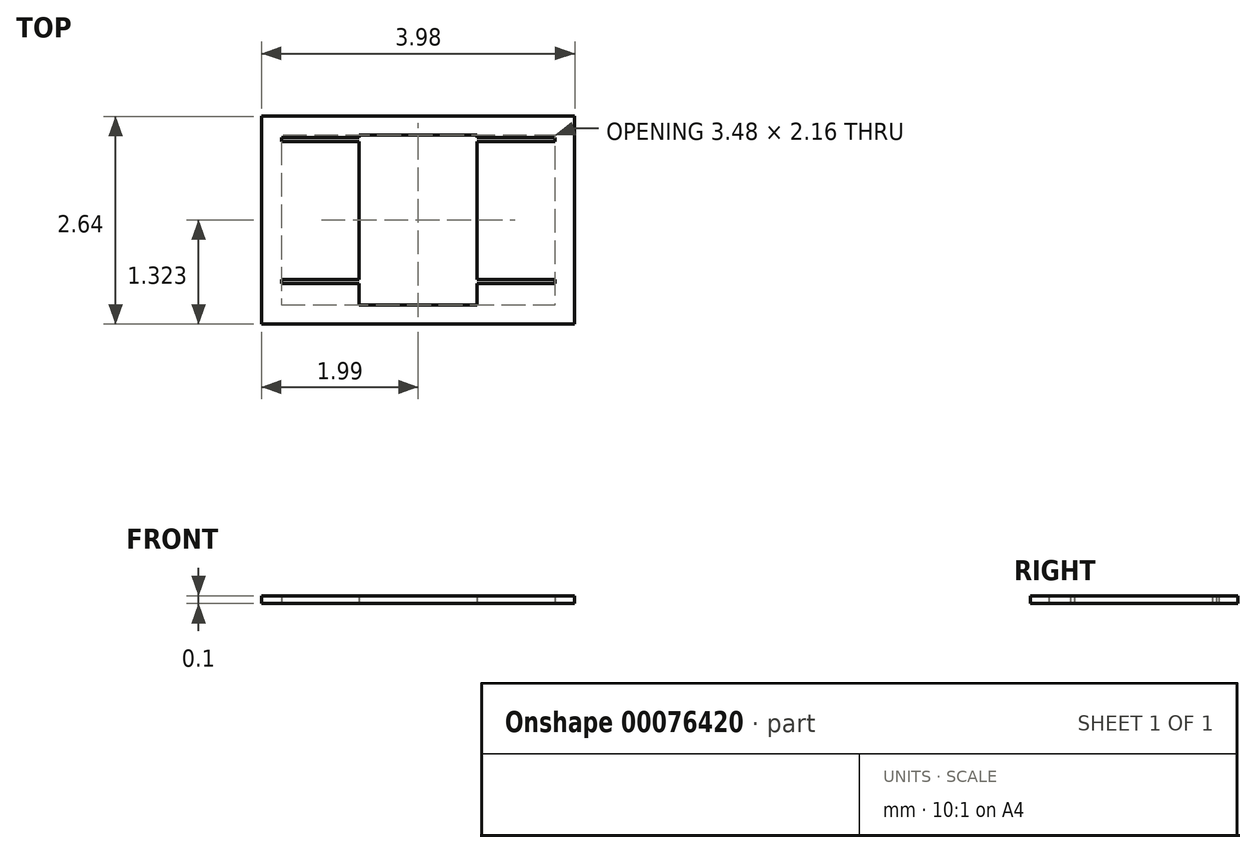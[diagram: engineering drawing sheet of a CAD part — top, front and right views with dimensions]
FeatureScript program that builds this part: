
annotation { "Feature Type Name" : "Feature", "Feature Type Description" : "" }
export const myFeature = defineFeature(function(context is Context, id is Id, definition is map)
    precondition{}
    {
        {
            var Q0;
            Q0=qCreatedBy(makeId("Top.planeOp"),FACE);
            var sketch = newSketch(context, id + "F0", { "sketchPlane" : qUnion([Q0])});
            skLineSegment(sketch, "E0", {"start": v(0.75, -1.22) * mm, "end": v(-0.75, -1.22) * mm});
            skLineSegment(sketch, "E1", {"start": v(0.75, -3.38) * mm, "end": v(0.75, -3.1) * mm});
            skLineSegment(sketch, "E2", {"start": v(-0.75, -1.22) * mm, "end": v(-0.75, -1.25) * mm});
            skLineSegment(sketch, "E3", {"start": v(-0.75, -3.38) * mm, "end": v(0.75, -3.38) * mm});
            skLineSegment(sketch, "E4", {"start": v(-1.74, -1.25) * mm, "end": v(-0.75, -1.25) * mm});
            skLineSegment(sketch, "E5", {"start": v(-1.74, -1.3) * mm, "end": v(-0.75, -1.3) * mm});
            skLineSegment(sketch, "E6", {"start": v(-0.75, -1.3) * mm, "end": v(-0.75, -3.05) * mm});
            skLineSegment(sketch, "E7", {"start": v(0.75, -1.25) * mm, "end": v(1.74, -1.25) * mm});
            skLineSegment(sketch, "E8", {"start": v(1.74, -1.3) * mm, "end": v(0.75, -1.3) * mm});
            skLineSegment(sketch, "E9", {"start": v(0.75, -1.25) * mm, "end": v(0.75, -1.22) * mm});
            skLineSegment(sketch, "E10", {"start": v(0.75, -3.05) * mm, "end": v(1.74, -3.05) * mm});
            skLineSegment(sketch, "E11", {"start": v(1.74, -3.1) * mm, "end": v(0.75, -3.1) * mm});
            skLineSegment(sketch, "E12", {"start": v(0.75, -3.05) * mm, "end": v(0.75, -1.3) * mm});
            skLineSegment(sketch, "E13", {"start": v(-0.75, -3.05) * mm, "end": v(-1.74, -3.05) * mm});
            skLineSegment(sketch, "E14", {"start": v(-1.74, -3.1) * mm, "end": v(-0.75, -3.1) * mm});
            skLineSegment(sketch, "E15", {"start": v(-0.75, -3.1) * mm, "end": v(-0.75, -3.38) * mm});
            skLineSegment(sketch, "E16", {"start": v(-1.74, -1.25) * mm, "end": v(-1.74, -1.3) * mm});
            skLineSegment(sketch, "E17", {"start": v(1.99, -0.98) * mm, "end": v(1.99, -3.62) * mm});
            skLineSegment(sketch, "E18", {"start": v(1.74, -1.25) * mm, "end": v(1.74, -1.3) * mm});
            skLineSegment(sketch, "E19", {"start": v(-1.99, -0.98) * mm, "end": v(1.99, -0.98) * mm});
            skLineSegment(sketch, "E20", {"start": v(-1.99, -0.98) * mm, "end": v(-1.99, -3.62) * mm});
            skLineSegment(sketch, "E21", {"start": v(-1.99, -3.62) * mm, "end": v(1.99, -3.62) * mm});
            skLineSegment(sketch, "E22", {"start": v(-1.74, -3.05) * mm, "end": v(-1.74, -3.1) * mm});
            skLineSegment(sketch, "E23", {"start": v(1.74, -3.05) * mm, "end": v(1.74, -3.1) * mm});
            skSolve(sketch);
        }
        {
            var Q0;
            Q0 = qSketchRegion(id + "F0", true);
            extrude(context, id + "F1", {"entities" : qUnion([Q0]), "depth" : .1 * mm});
        }
    });
